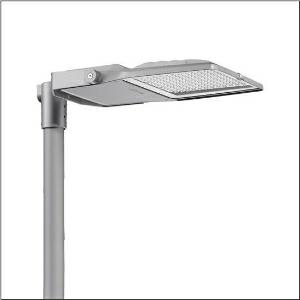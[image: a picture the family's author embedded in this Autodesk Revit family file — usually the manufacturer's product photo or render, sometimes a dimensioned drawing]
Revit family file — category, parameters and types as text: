
# Revit family: floodlight_fl_21_iq_midi___pl64_5xa7782f2e3a_4586
name_source: partatom
category: Lighting Fixtures
units: mm (PartAtom-declared; Revit-internal decimal feet)

## family parameters
Cut with Voids When Loaded = No
Host = Face
Light Source = No
Part Type = Normal
Room Calculation Point = No
Round Connector Dimension = Use Diameter
Shared = No

## types (1)
- --- (1 x LED, 34530 lm, 270.2 W, 3000K)
    Apparent Load = 270 VA
    CIE Flux Codes = 28 80 98 100 100
    Color Rendering = 70
    Color Temperature = 3000K
    Default Elevation = 1800 mm
    Description = Floodlight FL 21 iQ midi, floodlight, primary light control with lens, of PMMA, primary optical cover: protective disc, of toughened safety glass, transparent, light distribution: PL64, light emission: direct distribution, installation type: surface-mounted, LED, High Power LED, rated luminous flux: 34.530lm, luminous efficacy: 128lm/W, light colour: 730, colour temperature: 3000K, control gear: iQ Street-Remote/DALI, control: optimised constant luminous flux control (CLO 2.0), Desk-Remote (wireless, voltage-free reading and setting of iQ features in the workshop via application-optimized NFC function/RFID function), Smart-Wire, Night-Set, Temp-Guard, Auto-Match, Street-Remote, with terminal, 6-pole, mains connection: 220..240V, AC, 50/60Hz, start of lifetime: 270W, end of service life: 287W, reduction: 117W, luminaire housing, of diecast aluminium, powder-coated, Siteco® metallic grey (DB 702S), corrosivity category C5 mid according to DIN EN ISO 12944, suitable for swimming pools, chlorine-resistant, sealing non-destructively replaceable, please order mast flange separately, mast bracket, of steel, galvanised, powder-coated, Siteco® metallic grey (DB 702S), protection rating (complete): IP66, insulation class (complete): insulation class II (safety insulation), certification: CE, ENEC, VDE, protection symbol: D, impact resistance: IK08, permissible operating ambient temperature: -40..+40°C, permissible operating ambient temperature for outdoor applications: -40..+50°C, standard: DIN EN 12944, LABS conformity tested according to VDMA 24364:2018-05, packaging unit: 1 piece

Light Distribution: PL64
    Height = 76 mm
    Lamp = 1 x LED
    Lamp Light Flux = 34530 lm
    Lamp Power = 270.2 W
    Lamp count = 1
    Length = 657 mm
    Luminous efficacy = 128 lm/W
    Manufacturer = Siteco
    ModVariant = No
    Model = 5XA7782F2E3A
    Number of Poles = 1
    OnlyDefault = Yes
    Power Factor = 1
    Product Name = Floodlight FL 21 iQ midi | PL64
    Product group = floodlight | pylon annexe
    ProductGroupID = 6200
    Protection Class = Protection class II
    Protection Degree = IP 66
    RLX_Detail_Level = 1
    RLX_Emergency_Light_Flux = 0 lm
    RLX_Emergency_Type = 0
    RLX_Emergency_Type_DB = No
    RlxData = <blob elided: 153577 chars, md5=194a05ca>
    Socket = socket
    Standby Power = 0 W
    System Light Flux = 34530 lm
    System Power = 270 W
    Type Comments = factory setting: luminous flux: 100 % | dim-lin: 254 | 620 mA
    Type Image = l_1007123.jpg
    URL = http://relux.com
    VarID = @adj_106678
    Voltage = 0 V
    Weight = 0.00 kg
    Width = 442 mm

## geometry (parser evidence)
native form markers: Blend x4, Sweep x12
no freeform markers — native parametric forms only
